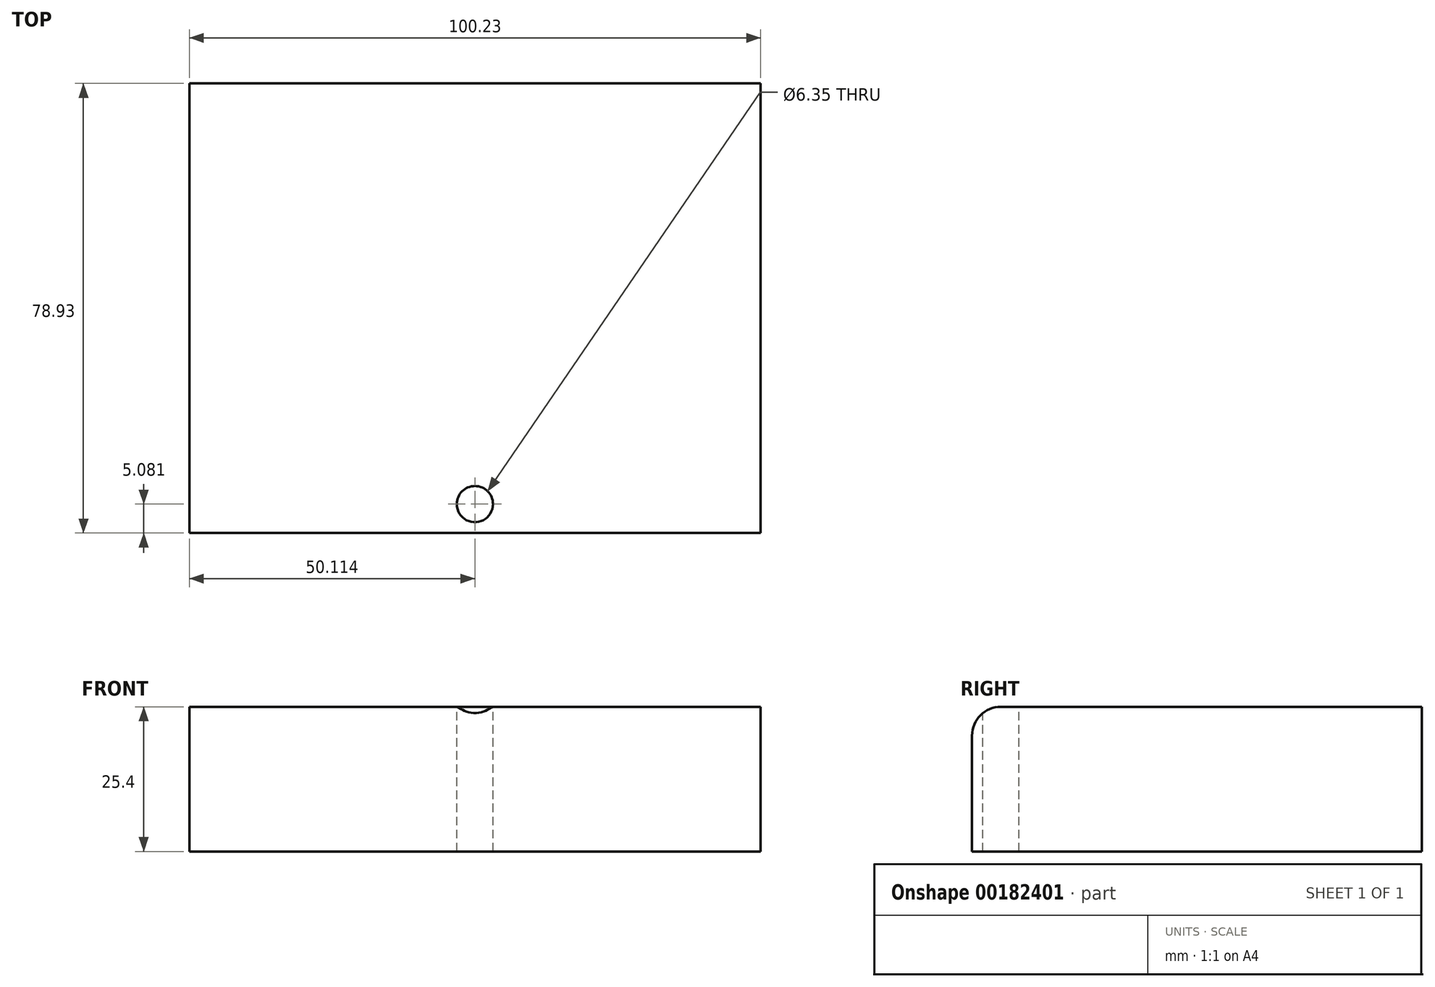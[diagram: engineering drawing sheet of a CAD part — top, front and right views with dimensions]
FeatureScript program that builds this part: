
annotation { "Feature Type Name" : "Feature", "Feature Type Description" : "" }
export const myFeature = defineFeature(function(context is Context, id is Id, definition is map)
    precondition{}
    {
        {
            var Q0;
            Q0=qCreatedBy(makeId("Top.planeOp"),FACE);
            var sketch = newSketch(context, id + "F0", { "sketchPlane" : qUnion([Q0])});
            skLineSegment(sketch, "E0.bottom", {"start": v(-57.08, -53.93) * mm, "end": v(43.15, -53.93) * mm});
            skLineSegment(sketch, "E0.top", {"start": v(-57.08, 25) * mm, "end": v(43.15, 25) * mm});
            skLineSegment(sketch, "E0.left", {"start": v(-57.08, -53.93) * mm, "end": v(-57.08, 25) * mm});
            skLineSegment(sketch, "E0.right", {"start": v(43.15, -53.93) * mm, "end": v(43.15, 25) * mm});
            skSolve(sketch);
        }
        {
            var Q0;
            Q0=makeQuery(id+"F0.imprint","IMPRINT",FACE,{"disambiguationData":[TD([[makeQuery(id+"F0.imprint","IMPRINT",EDGE,{"derivedFrom":sQuery(id+"F0.wireOp",EDGE,"E0.bottom")}),1.0]])]});
            extrude(context, id + "F1", {"entities" : qUnion([Q0]), "depth" : 25.4 * mm});
        }
        {
            var Q0;
            Q0=makeQuery(id+"F1.opExtrude","CAP_EDGE",EDGE,{"disambiguationData":[OSD([sQuery(id+"F0.wireOp",EDGE,"E0.bottom")])],"isStart":false});
            fillet(context, id + "F2", {"entities" : qUnion([Q0]), "radius" : 5.08 * mm, "tangentPropagation" : true, "allowEdgeOverflow" : false});
        }
        {
            var Q0;
            Q0=makeQuery(id+"F1.opExtrude","CAP_FACE",FACE,{"disambiguationData":[OSD([sQuery(id+"F0.wireOp",EDGE,"E0.bottom"),sQuery(id+"F0.wireOp",EDGE,"E0.top"),sQuery(id+"F0.wireOp",EDGE,"E0.left"),sQuery(id+"F0.wireOp",EDGE,"E0.right")])],"isStart":false});
            var sketch = newSketch(context, id + "F3", { "sketchPlane" : qUnion([Q0])});
            skSolve(sketch);
        }
        {
            var Q0;
            {var subQ0=sQuery(id+"F0.wireOp",EDGE,"E0.top");Q0=makeQuery(id+"F3.imprint","IMPRINT",FACE,{"disambiguationData":[TD([[makeQuery(id+"F3.imprint","IMPRINT",EDGE,{"derivedFrom":makeQuery(id+"F1.opExtrude","CAP_EDGE",EDGE,{"disambiguationData":[OSD([subQ0])],"isStart":false})}),-1.0]])]});}
            var sketch = newSketch(context, id + "F4", { "sketchPlane" : qUnion([Q0])});
            skPoint(sketch, "E1", {"position": v(-6.97, -48.85) * mm});
            skSolve(sketch);
        }
        {
            var Q0;
            Q0=sQuery(id+"F4.wireOp",VERTEX,"E1");
            var Q1;
            Q1=makeQuery(id+"F1.opExtrude","SWEPT_BODY",BODY,{"disambiguationData":[OSD([sQuery(id+"F0.wireOp",EDGE,"E0.bottom"),sQuery(id+"F0.wireOp",EDGE,"E0.top"),sQuery(id+"F0.wireOp",EDGE,"E0.left"),sQuery(id+"F0.wireOp",EDGE,"E0.right")])]});
            hole(context, id + "F5", {"style" : HoleStyle.SIMPLE, "endStyle" : HoleEndStyle.THROUGH, "holeDiameter" : 6.35 * mm, "locations" : qUnion([Q0]), "scope" : qUnion([Q1]), "isTappedThrough" : true});
        }
    });
